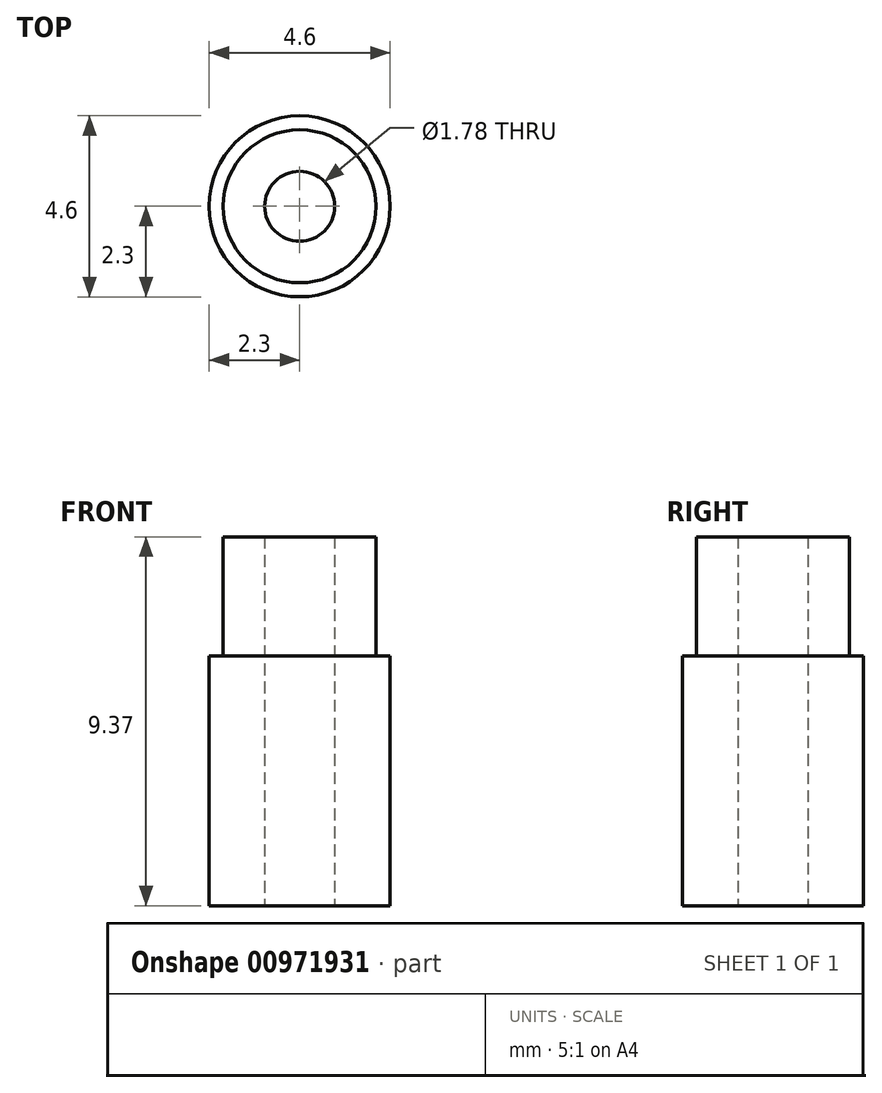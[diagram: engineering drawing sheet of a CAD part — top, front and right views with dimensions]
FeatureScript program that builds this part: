
annotation { "Feature Type Name" : "Feature", "Feature Type Description" : "" }
export const myFeature = defineFeature(function(context is Context, id is Id, definition is map)
    precondition{}
    {
        {
            var Q0;
            Q0=qCreatedBy(makeId("Top.planeOp"),FACE);
            cPlane(context, id + "F0", {"entities" : qUnion([Q0]), "cplaneType" : CPlaneType.OFFSET, "offset" : 6.35 * mm, "oppositeDirection" : true, "width" : 152.4 * mm, "height" : 152.4 * mm});
        }
        {
            var Q0;
            Q0=qCreatedBy(makeId("Top.planeOp"),FACE);
            var sketch = newSketch(context, id + "F1", { "sketchPlane" : qUnion([Q0])});
            skCircle(sketch, "E0", {"center": v(0, 0) * mm, "radius": 1.94 * mm});
            skCircle(sketch, "E1", {"center": v(0, 0) * mm, "radius": 2.3 * mm});
            skSolve(sketch);
        }
        {
            var Q0;
            Q0=makeQuery(id+"F1.imprint","IMPRINT",FACE,{"disambiguationData":[TD([[makeQuery(id+"F1.imprint","IMPRINT",EDGE,{"derivedFrom":sQuery(id+"F1.wireOp",EDGE,"E0")}),1.0]])]});
            extrude(context, id + "F2", {"entities" : qUnion([Q0]), "depth" : 3.02 * mm, "offsetDistance" : 25.4 * mm});
        }
        {
            var Q0;
            Q0=makeQuery(id+"F1.imprint","IMPRINT",FACE,{"disambiguationData":[TD([[makeQuery(id+"F1.imprint","IMPRINT",EDGE,{"derivedFrom":sQuery(id+"F1.wireOp",EDGE,"E0")}),-1.0]])]});
            var Q1;
            Q1=makeQuery(id+"F1.imprint","IMPRINT",FACE,{"disambiguationData":[TD([[makeQuery(id+"F1.imprint","IMPRINT",EDGE,{"derivedFrom":sQuery(id+"F1.wireOp",EDGE,"E0")}),1.0]])]});
            extrude(context, id + "F3", {"entities" : qUnion([Q0, Q1]), "operationType" : NewBodyOperationType.ADD, "oppositeDirection" : true, "depth" : 6.35 * mm, "offsetDistance" : 25.4 * mm});
        }
        {
            var Q0;
            Q0=qCreatedBy(id+"F0.planeOp",FACE);
            var sketch = newSketch(context, id + "F4", { "sketchPlane" : qUnion([Q0])});
            skPoint(sketch, "E2", {"position": v(0, 0) * mm});
            skSolve(sketch);
        }
        {
            var Q0;
            Q0=sQuery(id+"F4.wireOp",VERTEX,"E2");
            var Q1;
            Q1=makeQuery(id+"F2.opExtrude","SWEPT_BODY",BODY,{"disambiguationData":[OSD([sQuery(id+"F1.wireOp",EDGE,"E0")])]});
            hole(context, id + "F5", {"style" : HoleStyle.SIMPLE, "endStyle" : HoleEndStyle.THROUGH, "oppositeDirection" : true, "standardTappedOrClearance" : lookupTablePath({ "standard" : "ANSI", "engagement" : "75%", "pitch" : "56 tpi", "size" : "#2", "type" : "Tapped" }), "standardBlindInLast" : lookupTablePath({ "standard" : "ANSI", "fit" : "Normal", "engagement" : "75%", "pitch" : "56 tpi", "size" : "#2", "type" : "Clearance & tapped" }), "holeDiameter" : 1.78 * mm, "majorDiameter" : 2.18 * mm, "showTappedDepth" : true, "isTappedThrough" : true, "tappedDepth" : 1.81 * mm, "tapClearance" : 3, "startFromSketch" : true, "locations" : qUnion([Q0]), "scope" : qUnion([Q1])});
        }
    });
